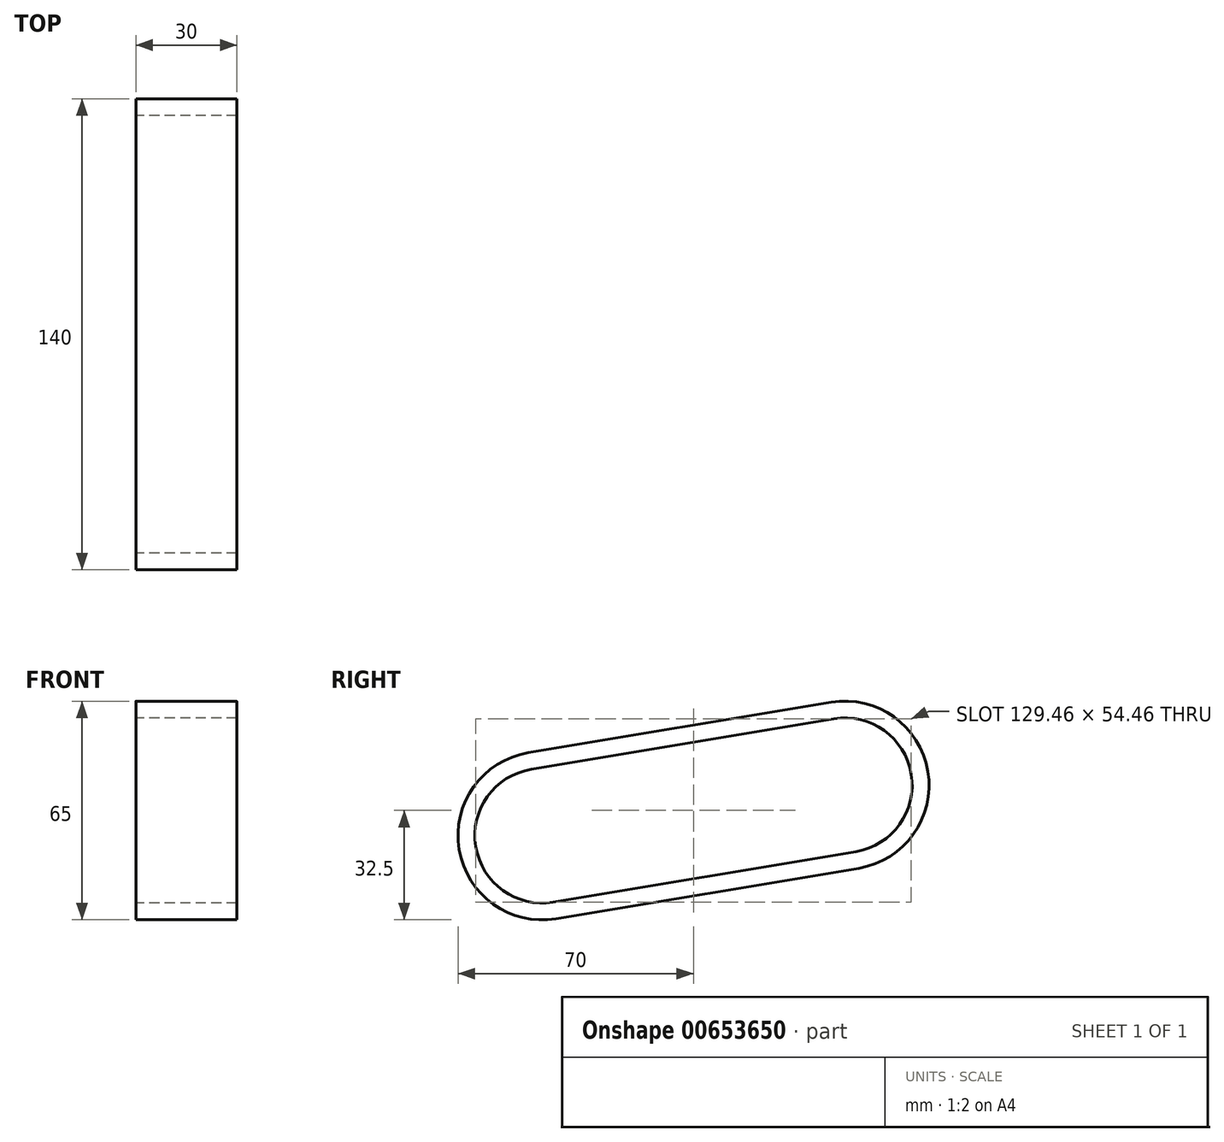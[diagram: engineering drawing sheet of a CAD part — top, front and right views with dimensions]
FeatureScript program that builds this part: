
annotation { "Feature Type Name" : "Feature", "Feature Type Description" : "" }
export const myFeature = defineFeature(function(context is Context, id is Id, definition is map)
    precondition{}
    {
        {
            var Q0;
            Q0=qCreatedBy(makeId("Right.planeOp"),FACE);
            var sketch = newSketch(context, id + "F0", { "sketchPlane" : qUnion([Q0])});
            skArc(sketch, "E0", {"start": v(56.71, 79.73) * mm, "mid": v(40.27, 56.71) * mm, "end": v(63.29, 40.27) * mm});
            skArc(sketch, "E1", {"start": v(153.29, 55.27) * mm, "mid": v(169.73, 78.29) * mm, "end": v(146.71, 94.73) * mm});
            skLineSegment(sketch, "E2.bottom", {"start": v(0, 110) * mm, "end": v(200, 110) * mm});
            skLineSegment(sketch, "E2.top", {"start": v(0, 0) * mm, "end": v(200, 0) * mm});
            skLineSegment(sketch, "E2.left", {"start": v(0, 110) * mm, "end": v(0, 0) * mm});
            skLineSegment(sketch, "E2.right", {"start": v(200, 110) * mm, "end": v(200, 0) * mm});
            skLineSegment(sketch, "E3", {"start": v(56.71, 79.73) * mm, "end": v(146.71, 94.73) * mm});
            skLineSegment(sketch, "E4", {"start": v(63.29, 40.27) * mm, "end": v(153.29, 55.27) * mm});
            skLineSegment(sketch, "E5.0", {"start": v(64.1, 35.34) * mm, "end": v(154.1, 50.34) * mm});
            skArc(sketch, "E5.1", {"start": v(55.9, 84.66) * mm, "mid": v(35.34, 55.9) * mm, "end": v(64.1, 35.34) * mm});
            skLineSegment(sketch, "E5.2", {"start": v(55.9, 84.66) * mm, "end": v(145.9, 99.66) * mm});
            skArc(sketch, "E5.3", {"start": v(154.1, 50.34) * mm, "mid": v(174.66, 79.1) * mm, "end": v(145.9, 99.66) * mm});
            skSolve(sketch);
        }
        {
            var Q0;
            Q0=makeQuery(id+"F0.imprint","IMPRINT",FACE,{"disambiguationData":[TD([[makeQuery(id+"F0.imprint","IMPRINT",EDGE,{"derivedFrom":sQuery(id+"F0.wireOp",EDGE,"E0")}),-1.0]])]});
            extrude(context, id + "F1", {"entities" : qUnion([Q0]), "depth" : 30 * mm, "offsetDistance" : 25 * mm});
        }
    });
